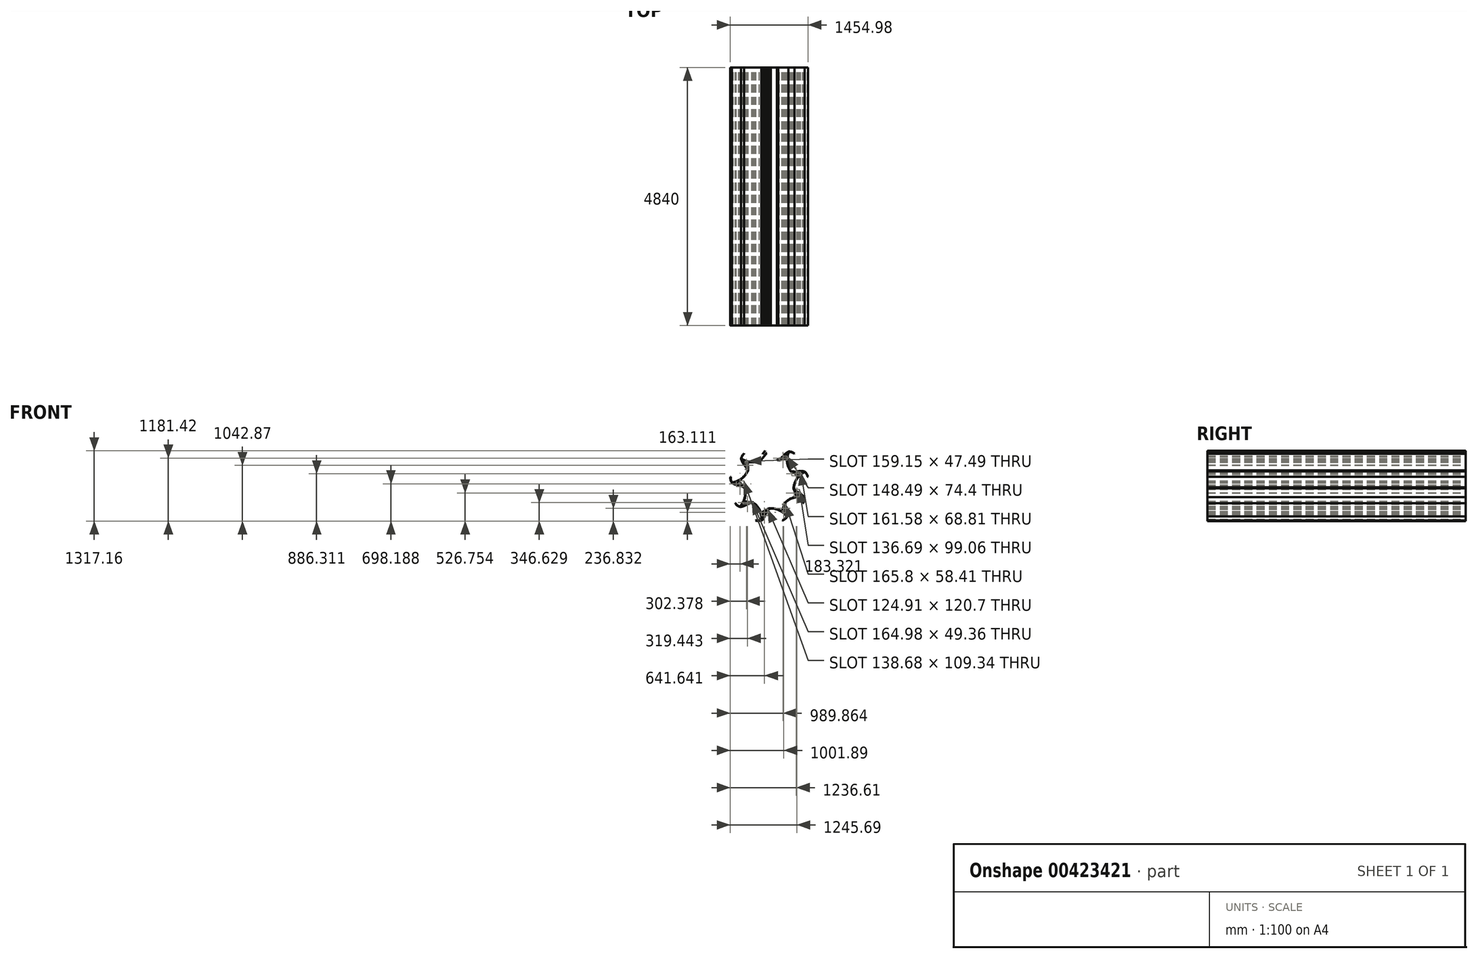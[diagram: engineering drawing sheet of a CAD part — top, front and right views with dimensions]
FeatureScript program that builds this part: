
annotation { "Feature Type Name" : "Feature", "Feature Type Description" : "" }
export const myFeature = defineFeature(function(context is Context, id is Id, definition is map)
    precondition{}
    {
        {
            var Q0;
            Q0=qCreatedBy(makeId("Front.planeOp"),FACE);
            var sketch = newSketch(context, id + "F0", { "sketchPlane" : qUnion([Q0])});
            skCircle(sketch, "E0", {"center": v(0, 0) * mm, "radius": 462.5 * mm, "construction": true});
            skLineSegment(sketch, "E1", {"start": v(0, 0) * mm, "end": v(0, 462.5) * mm, "construction": true});
            skPoint(sketch, "E2", {"position": v(0, 737.5) * mm});
            skPoint(sketch, "E3", {"position": v(-110, 692.5) * mm});
            skPoint(sketch, "E4", {"position": v(0, 729.5) * mm});
            skPoint(sketch, "E5", {"position": v(-97, 692.5) * mm});
            skPoint(sketch, "E6", {"position": v(-172.02, 429.32) * mm});
            skLineSegment(sketch, "E7", {"start": v(0, 0) * mm, "end": v(-172.02, 429.32) * mm, "construction": true});
            skLineSegment(sketch, "E8", {"start": v(-172.02, 429.32) * mm, "end": v(-176.48, 440.46) * mm, "construction": true});
            skPoint(sketch, "E9", {"position": v(-174.25, 434.9) * mm});
            skArc(sketch, "E10", {"start": v(-174.25, 434.9) * mm, "mid": v(-160.23, 440.25) * mm, "end": v(-146.06, 445.15) * mm});
            skArc(sketch, "E11", {"start": v(-176.48, 440.46) * mm, "mid": v(-166.98, 444.15) * mm, "end": v(-157.4, 447.63) * mm});
            skLineSegment(sketch, "E12", {"start": v(-176.48, 440.46) * mm, "end": v(-174.25, 434.9) * mm});
            skLineSegment(sketch, "E13", {"start": v(0, 0) * mm, "end": v(-146.06, 445.15) * mm, "construction": true});
            skLineSegment(sketch, "E14", {"start": v(-146.06, 445.15) * mm, "end": v(-148.66, 453.08) * mm, "construction": true});
            skPoint(sketch, "E15.MirrorP", {"position": v(172.02, 429.32) * mm});
            skPoint(sketch, "E16.MirrorP", {"position": v(174.25, 434.9) * mm});
            skLineSegment(sketch, "E17.MirrorCS", {"start": v(146.06, 445.15) * mm, "end": v(148.66, 453.08) * mm, "construction": true});
            skLineSegment(sketch, "E18.MirrorCS", {"start": v(172.02, 429.32) * mm, "end": v(176.48, 440.46) * mm, "construction": true});
            skLineSegment(sketch, "E19.MirrorCS", {"start": v(0, 0) * mm, "end": v(172.02, 429.32) * mm, "construction": true});
            skLineSegment(sketch, "E20.MirrorCS", {"start": v(0, 0) * mm, "end": v(146.06, 445.15) * mm, "construction": true});
            skArc(sketch, "E21", {"start": v(146.06, 445.15) * mm, "mid": v(160.23, 440.25) * mm, "end": v(174.25, 434.9) * mm});
            skLineSegment(sketch, "E22", {"start": v(174.25, 434.9) * mm, "end": v(172.02, 429.32) * mm});
            skPoint(sketch, "E23", {"position": v(131.78, 443.33) * mm});
            skPoint(sketch, "E24", {"position": v(144.19, 439.45) * mm});
            skArc(sketch, "E25", {"start": v(131.78, 443.33) * mm, "mid": v(152.06, 436.79) * mm, "end": v(172.02, 429.32) * mm});
            skLineSegment(sketch, "E26", {"start": v(-157.4, 692.5) * mm, "end": v(-110, 692.5) * mm, "construction": true});
            skPoint(sketch, "E27", {"position": v(-133.7, 692.5) * mm});
            skLineSegment(sketch, "E28", {"start": v(-157.4, 692.5) * mm, "end": v(-157.4, 447.63) * mm, "construction": true});
            skPoint(sketch, "E29", {"position": v(-157.4, 570.07) * mm});
            skPoint(sketch, "E30", {"position": v(-133.7, 570.07) * mm});
            skArc(sketch, "E31", {"start": v(-157.4, 447.63) * mm, "mid": v(-139.68, 507.71) * mm, "end": v(-133.7, 570.07) * mm});
            skArc(sketch, "E32", {"start": v(-110, 692.5) * mm, "mid": v(-127.72, 632.42) * mm, "end": v(-133.7, 570.07) * mm});
            skArc(sketch, "E33", {"start": v(0, 737.5) * mm, "mid": v(-59.42, 725.82) * mm, "end": v(-110, 692.5) * mm});
            skLineSegment(sketch, "E34", {"start": v(0, 737.5) * mm, "end": v(0, 729.5) * mm});
            skArc(sketch, "E35", {"start": v(0, 729.5) * mm, "mid": v(-51.9, 719.94) * mm, "end": v(-97, 692.5) * mm});
            skArc(sketch, "E36", {"start": v(-97, 692.5) * mm, "mid": v(-5.55, 539.27) * mm, "end": v(146.06, 445.15) * mm});
            skArc(sketch, "E37", {"start": v(-146.06, 445.15) * mm, "mid": v(-127.1, 506.34) * mm, "end": v(-120.7, 570.07) * mm});
            skArc(sketch, "E38", {"start": v(-103.63, 668.34) * mm, "mid": v(-116.4, 619.94) * mm, "end": v(-120.7, 570.07) * mm});
            skPoint(sketch, "E39", {"position": v(-118.63, 668.34) * mm});
            skPoint(sketch, "E40", {"position": v(-88.63, 668.34) * mm});
            skLineSegment(sketch, "E41", {"start": v(-118.63, 668.34) * mm, "end": v(-88.63, 668.34) * mm, "construction": true});
            skArc(sketch, "E42", {"start": v(-103.63, 668.34) * mm, "mid": v(-10.1, 530.54) * mm, "end": v(131.78, 443.33) * mm});
            skLineSegment(sketch, "E43", {"start": v(-146.06, 445.15) * mm, "end": v(-47.75, 572) * mm});
            skLineSegment(sketch, "E44", {"start": v(-50.29, 575.26) * mm, "end": v(-140.74, 458.55) * mm});
            skLineSegment(sketch, "E45", {"start": v(-121.26, 551.05) * mm, "end": v(-74.81, 611) * mm});
            skLineSegment(sketch, "E46", {"start": v(-120.92, 558.02) * mm, "end": v(-77.02, 614.67) * mm});
            skPoint(sketch, "E47.1.0", {"position": v(-520.48, 435.72) * mm});
            skPoint(sketch, "E47.1.1", {"position": v(-547.55, 444.55) * mm});
            skArc(sketch, "E47.1.2", {"start": v(-474.06, 564.96) * mm, "mid": v(-512.07, 517.8) * mm, "end": v(-529.4, 459.78) * mm});
            skPoint(sketch, "E47.1.3", {"position": v(-468.91, 558.83) * mm});
            skLineSegment(sketch, "E47.1.5", {"start": v(-398.02, 247.12) * mm, "end": v(-404.26, 407.48) * mm});
            skArc(sketch, "E47.1.6", {"start": v(-398.02, 247.12) * mm, "mid": v(-422.83, 306.18) * mm, "end": v(-458.9, 359.11) * mm});
            skPoint(sketch, "E47.1.7", {"position": v(-497.5, 455) * mm});
            skPoint(sketch, "E47.1.8", {"position": v(-413.02, 221.14) * mm});
            skLineSegment(sketch, "E47.1.9", {"start": v(-447.1, 344.18) * mm, "end": v(-450.05, 419.96) * mm});
            skPoint(sketch, "E47.1.10", {"position": v(-474.06, 564.96) * mm});
            skArc(sketch, "E47.1.11", {"start": v(-519.44, 468.14) * mm, "mid": v(-350.89, 409.54) * mm, "end": v(-174.25, 434.89) * mm});
            skPoint(sketch, "E47.1.12", {"position": v(-487, 335.53) * mm});
            skLineSegment(sketch, "E47.1.13", {"start": v(-565.7, 429.31) * mm, "end": v(-408.3, 241.74) * mm, "construction": true});
            skPoint(sketch, "E47.1.14", {"position": v(-146.06, 445.15) * mm});
            skLineSegment(sketch, "E47.1.15", {"start": v(-408.3, 408.35) * mm, "end": v(-402.56, 260.8) * mm});
            skArc(sketch, "E47.1.16", {"start": v(-509, 445.37) * mm, "mid": v(-348.77, 399.92) * mm, "end": v(-184.02, 424.31) * mm});
            skArc(sketch, "E47.1.17", {"start": v(-529.4, 459.78) * mm, "mid": v(-504.35, 402.37) * mm, "end": v(-468.85, 350.76) * mm});
            skPoint(sketch, "E47.1.18", {"position": v(-529.4, 459.78) * mm});
            skPoint(sketch, "E47.1.19", {"position": v(-184.02, 424.31) * mm});
            skPoint(sketch, "E47.1.20", {"position": v(-468.85, 350.76) * mm});
            skPoint(sketch, "E47.1.21", {"position": v(-519.44, 468.14) * mm});
            skArc(sketch, "E47.1.22", {"start": v(-509, 445.37) * mm, "mid": v(-487.66, 400.08) * mm, "end": v(-458.9, 359.11) * mm});
            skLineSegment(sketch, "E47.1.23", {"start": v(-451.32, 349.74) * mm, "end": v(-454.1, 421.35) * mm});
            skArc(sketch, "E47.1.24", {"start": v(-408.3, 241.74) * mm, "mid": v(-433.35, 299.15) * mm, "end": v(-468.85, 350.76) * mm});
            skArc(sketch, "E47.1.25", {"start": v(-468.91, 558.83) * mm, "mid": v(-502.53, 518.14) * mm, "end": v(-519.44, 468.14) * mm});
            skPoint(sketch, "E47.1.26", {"position": v(-407.73, 218.31) * mm});
            skLineSegment(sketch, "E47.1.27", {"start": v(-565.7, 429.31) * mm, "end": v(-529.4, 459.78) * mm, "construction": true});
            skPoint(sketch, "E47.1.28", {"position": v(-144.2, 439.45) * mm});
            skLineSegment(sketch, "E47.1.29", {"start": v(-520.48, 435.72) * mm, "end": v(-497.5, 455) * mm, "construction": true});
            skArc(sketch, "E47.1.30", {"start": v(-184.02, 424.31) * mm, "mid": v(-164.28, 432.34) * mm, "end": v(-144.2, 439.45) * mm});
            skLineSegment(sketch, "E47.1.31", {"start": v(-474.06, 564.96) * mm, "end": v(-468.91, 558.83) * mm});
            skArc(sketch, "E47.1.32", {"start": v(-174.25, 434.89) * mm, "mid": v(-160.24, 440.24) * mm, "end": v(-146.06, 445.15) * mm});
            skLineSegment(sketch, "E47.1.33", {"start": v(-407.73, 218.31) * mm, "end": v(-418.31, 223.97) * mm, "construction": true});
            skArc(sketch, "E47.1.34", {"start": v(-418.31, 223.97) * mm, "mid": v(-413.4, 232.9) * mm, "end": v(-408.3, 241.74) * mm});
            skArc(sketch, "E47.1.35", {"start": v(-413.02, 221.14) * mm, "mid": v(-405.73, 234.25) * mm, "end": v(-398.02, 247.12) * mm});
            skLineSegment(sketch, "E47.1.36", {"start": v(-418.31, 223.97) * mm, "end": v(-413.02, 221.14) * mm});
            skLineSegment(sketch, "E47.1.37", {"start": v(-174.25, 434.89) * mm, "end": v(-177.36, 442.64) * mm, "construction": true});
            skLineSegment(sketch, "E47.1.38", {"start": v(-398.02, 247.12) * mm, "end": v(-405.12, 251.53) * mm, "construction": true});
            skLineSegment(sketch, "E47.1.39", {"start": v(-146.06, 445.15) * mm, "end": v(-144.2, 439.45) * mm});
            skLineSegment(sketch, "E47.1.40", {"start": v(-144.2, 439.45) * mm, "end": v(-147.93, 450.85) * mm, "construction": true});
            skPoint(sketch, "E47.2.0", {"position": v(-678.8, -0.78) * mm});
            skPoint(sketch, "E47.2.1", {"position": v(-705.2, -11.42) * mm});
            skArc(sketch, "E47.2.2", {"start": v(-726.3, 128.07) * mm, "mid": v(-725.1, 67.51) * mm, "end": v(-701.08, 11.92) * mm});
            skPoint(sketch, "E47.2.3", {"position": v(-718.42, 126.68) * mm});
            skPoint(sketch, "E47.2.4", {"position": v(-407.74, 218.3) * mm});
            skLineSegment(sketch, "E47.2.5", {"start": v(-463.75, -66.54) * mm, "end": v(-571.6, 52.3) * mm});
            skArc(sketch, "E47.2.6", {"start": v(-463.75, -66.54) * mm, "mid": v(-520.71, -37.25) * mm, "end": v(-582.37, -19.87) * mm});
            skPoint(sketch, "E47.2.7", {"position": v(-673.58, 28.77) * mm});
            skPoint(sketch, "E47.2.8", {"position": v(-458.54, -96.08) * mm});
            skLineSegment(sketch, "E47.2.9", {"start": v(-563.73, -23.73) * mm, "end": v(-614.7, 32.42) * mm});
            skPoint(sketch, "E47.2.10", {"position": v(-726.3, 128.07) * mm});
            skArc(sketch, "E47.2.11", {"start": v(-698.82, 24.73) * mm, "mid": v(-532.04, 88.18) * mm, "end": v(-413.03, 221.14) * mm});
            skPoint(sketch, "E47.2.12", {"position": v(-588.74, -56.01) * mm});
            skLineSegment(sketch, "E47.2.13", {"start": v(-709.31, -34.75) * mm, "end": v(-468.17, -77.27) * mm, "construction": true});
            skPoint(sketch, "E47.2.14", {"position": v(-398.03, 247.12) * mm});
            skLineSegment(sketch, "E47.2.15", {"start": v(-575.25, 50.37) * mm, "end": v(-476.02, -58.97) * mm});
            skArc(sketch, "E47.2.16", {"start": v(-676.19, 14) * mm, "mid": v(-524.24, 82.18) * mm, "end": v(-413.71, 206.76) * mm});
            skArc(sketch, "E47.2.17", {"start": v(-701.08, 11.92) * mm, "mid": v(-645, -15.96) * mm, "end": v(-584.62, -32.68) * mm});
            skPoint(sketch, "E47.2.18", {"position": v(-701.08, 11.92) * mm});
            skPoint(sketch, "E47.2.19", {"position": v(-413.71, 206.76) * mm});
            skPoint(sketch, "E47.2.20", {"position": v(-584.62, -32.68) * mm});
            skPoint(sketch, "E47.2.21", {"position": v(-698.82, 24.73) * mm});
            skArc(sketch, "E47.2.22", {"start": v(-676.19, 14) * mm, "mid": v(-630.74, -6.98) * mm, "end": v(-582.37, -19.87) * mm});
            skLineSegment(sketch, "E47.2.23", {"start": v(-570.54, -22.19) * mm, "end": v(-618.7, 30.88) * mm});
            skArc(sketch, "E47.2.24", {"start": v(-468.17, -77.27) * mm, "mid": v(-524.26, -49.4) * mm, "end": v(-584.62, -32.68) * mm});
            skArc(sketch, "E47.2.25", {"start": v(-718.42, 126.68) * mm, "mid": v(-718.01, 73.9) * mm, "end": v(-698.82, 24.73) * mm});
            skPoint(sketch, "E47.2.26", {"position": v(-452.67, -94.85) * mm});
            skLineSegment(sketch, "E47.2.27", {"start": v(-709.31, -34.75) * mm, "end": v(-701.08, 11.92) * mm, "construction": true});
            skPoint(sketch, "E47.2.28", {"position": v(-392.93, 243.95) * mm});
            skLineSegment(sketch, "E47.2.29", {"start": v(-678.8, -0.78) * mm, "end": v(-673.58, 28.77) * mm, "construction": true});
            skArc(sketch, "E47.2.30", {"start": v(-413.71, 206.76) * mm, "mid": v(-403.75, 225.6) * mm, "end": v(-392.93, 243.95) * mm});
            skLineSegment(sketch, "E47.2.31", {"start": v(-726.3, 128.07) * mm, "end": v(-718.42, 126.68) * mm});
            skArc(sketch, "E47.2.32", {"start": v(-413.03, 221.14) * mm, "mid": v(-405.73, 234.25) * mm, "end": v(-398.03, 247.12) * mm});
            skLineSegment(sketch, "E47.2.33", {"start": v(-452.67, -94.85) * mm, "end": v(-464.41, -97.31) * mm, "construction": true});
            skArc(sketch, "E47.2.34", {"start": v(-464.41, -97.31) * mm, "mid": v(-466.4, -87.31) * mm, "end": v(-468.17, -77.27) * mm});
            skArc(sketch, "E47.2.35", {"start": v(-458.54, -96.08) * mm, "mid": v(-461.38, -81.35) * mm, "end": v(-463.75, -66.54) * mm});
            skLineSegment(sketch, "E47.2.36", {"start": v(-464.41, -97.31) * mm, "end": v(-458.54, -96.08) * mm});
            skLineSegment(sketch, "E47.2.37", {"start": v(-413.03, 221.14) * mm, "end": v(-420.39, 225.08) * mm, "construction": true});
            skLineSegment(sketch, "E47.2.38", {"start": v(-463.75, -66.54) * mm, "end": v(-472.02, -67.72) * mm, "construction": true});
            skLineSegment(sketch, "E47.2.39", {"start": v(-398.03, 247.12) * mm, "end": v(-392.93, 243.95) * mm});
            skLineSegment(sketch, "E47.2.40", {"start": v(-392.93, 243.95) * mm, "end": v(-403.12, 250.28) * mm, "construction": true});
            skPoint(sketch, "E47.3.0", {"position": v(-519.49, -436.91) * mm});
            skPoint(sketch, "E47.3.1", {"position": v(-532.87, -462.04) * mm});
            skArc(sketch, "E47.3.2", {"start": v(-638.7, -368.75) * mm, "mid": v(-598.86, -414.37) * mm, "end": v(-544.72, -441.51) * mm});
            skPoint(sketch, "E47.3.3", {"position": v(-631.77, -364.75) * mm});
            skPoint(sketch, "E47.3.4", {"position": v(-452.67, -94.86) * mm});
            skLineSegment(sketch, "E47.3.5", {"start": v(-312.48, -349.06) * mm, "end": v(-471.5, -327.36) * mm});
            skArc(sketch, "E47.3.6", {"start": v(-312.48, -349.06) * mm, "mid": v(-374.95, -363.24) * mm, "end": v(-433.34, -389.56) * mm});
            skPoint(sketch, "E47.3.7", {"position": v(-534.49, -410.93) * mm});
            skPoint(sketch, "E47.3.8", {"position": v(-289.5, -368.35) * mm});
            skLineSegment(sketch, "E47.3.9", {"start": v(-416.6, -380.54) * mm, "end": v(-491.73, -370.28) * mm});
            skPoint(sketch, "E47.3.10", {"position": v(-638.7, -368.75) * mm});
            skArc(sketch, "E47.3.11", {"start": v(-551.22, -430.25) * mm, "mid": v(-464.25, -274.44) * mm, "end": v(-458.54, -96.09) * mm});
            skPoint(sketch, "E47.3.12", {"position": v(-415, -421.34) * mm});
            skLineSegment(sketch, "E47.3.13", {"start": v(-521.02, -482.56) * mm, "end": v(-308.97, -360.13) * mm, "construction": true});
            skPoint(sketch, "E47.3.14", {"position": v(-463.75, -66.54) * mm});
            skLineSegment(sketch, "E47.3.15", {"start": v(-473.05, -331.18) * mm, "end": v(-326.75, -351.15) * mm});
            skArc(sketch, "E47.3.16", {"start": v(-526.99, -423.92) * mm, "mid": v(-454.41, -274.02) * mm, "end": v(-449.82, -107.54) * mm});
            skArc(sketch, "E47.3.17", {"start": v(-544.72, -441.51) * mm, "mid": v(-483.83, -426.82) * mm, "end": v(-426.84, -400.82) * mm});
            skPoint(sketch, "E47.3.18", {"position": v(-544.72, -441.51) * mm});
            skPoint(sketch, "E47.3.19", {"position": v(-449.82, -107.54) * mm});
            skPoint(sketch, "E47.3.20", {"position": v(-426.84, -400.82) * mm});
            skPoint(sketch, "E47.3.21", {"position": v(-551.22, -430.25) * mm});
            skArc(sketch, "E47.3.22", {"start": v(-526.99, -423.92) * mm, "mid": v(-478.68, -410.78) * mm, "end": v(-433.34, -389.56) * mm});
            skLineSegment(sketch, "E47.3.23", {"start": v(-422.8, -383.73) * mm, "end": v(-493.8, -374.04) * mm});
            skArc(sketch, "E47.3.24", {"start": v(-308.97, -360.13) * mm, "mid": v(-369.86, -374.82) * mm, "end": v(-426.84, -400.82) * mm});
            skArc(sketch, "E47.3.25", {"start": v(-631.77, -364.75) * mm, "mid": v(-597.53, -404.92) * mm, "end": v(-551.22, -430.25) * mm});
            skPoint(sketch, "E47.3.26", {"position": v(-285.8, -363.63) * mm});
            skLineSegment(sketch, "E47.3.27", {"start": v(-521.02, -482.56) * mm, "end": v(-544.72, -441.51) * mm, "construction": true});
            skPoint(sketch, "E47.3.28", {"position": v(-457.81, -65.7) * mm});
            skLineSegment(sketch, "E47.3.29", {"start": v(-519.49, -436.91) * mm, "end": v(-534.49, -410.93) * mm, "construction": true});
            skArc(sketch, "E47.3.30", {"start": v(-449.82, -107.54) * mm, "mid": v(-454.3, -86.7) * mm, "end": v(-457.81, -65.7) * mm});
            skLineSegment(sketch, "E47.3.31", {"start": v(-638.7, -368.75) * mm, "end": v(-631.77, -364.75) * mm});
            skArc(sketch, "E47.3.32", {"start": v(-458.54, -96.09) * mm, "mid": v(-461.38, -81.36) * mm, "end": v(-463.75, -66.54) * mm});
            skLineSegment(sketch, "E47.3.33", {"start": v(-285.8, -363.63) * mm, "end": v(-293.21, -373.07) * mm, "construction": true});
            skArc(sketch, "E47.3.34", {"start": v(-293.21, -373.07) * mm, "mid": v(-301.16, -366.68) * mm, "end": v(-308.97, -360.13) * mm});
            skArc(sketch, "E47.3.35", {"start": v(-289.5, -368.35) * mm, "mid": v(-301.15, -358.89) * mm, "end": v(-312.48, -349.06) * mm});
            skLineSegment(sketch, "E47.3.36", {"start": v(-293.21, -373.07) * mm, "end": v(-289.5, -368.35) * mm});
            skLineSegment(sketch, "E47.3.37", {"start": v(-458.54, -96.09) * mm, "end": v(-466.71, -97.8) * mm, "construction": true});
            skLineSegment(sketch, "E47.3.38", {"start": v(-312.48, -349.06) * mm, "end": v(-318.05, -355.28) * mm, "construction": true});
            skLineSegment(sketch, "E47.3.39", {"start": v(-463.75, -66.54) * mm, "end": v(-457.81, -65.7) * mm});
            skLineSegment(sketch, "E47.3.40", {"start": v(-457.81, -65.7) * mm, "end": v(-469.69, -67.4) * mm, "construction": true});
            skPoint(sketch, "E47.4.0", {"position": v(-117.1, -668.61) * mm});
            skPoint(sketch, "E47.4.1", {"position": v(-111.21, -696.46) * mm});
            skArc(sketch, "E47.4.2", {"start": v(-252.24, -693.02) * mm, "mid": v(-192.4, -702.37) * mm, "end": v(-133.48, -688.36) * mm});
            skPoint(sketch, "E47.4.3", {"position": v(-249.5, -685.5) * mm});
            skPoint(sketch, "E47.4.4", {"position": v(-285.8, -363.63) * mm});
            skLineSegment(sketch, "E47.4.5", {"start": v(-15, -468.26) * mm, "end": v(-150.76, -553.84) * mm});
            skArc(sketch, "E47.4.6", {"start": v(-15, -468.26) * mm, "mid": v(-53.74, -519.27) * mm, "end": v(-81.56, -576.97) * mm});
            skPoint(sketch, "E47.4.7", {"position": v(-145.3, -658.35) * mm});
            skPoint(sketch, "E47.4.8", {"position": v(15, -468.26) * mm});
            skLineSegment(sketch, "E47.4.9", {"start": v(-74.52, -559.3) * mm, "end": v(-138.67, -599.73) * mm});
            skPoint(sketch, "E47.4.10", {"position": v(-252.24, -693.02) * mm});
            skArc(sketch, "E47.4.11", {"start": v(-145.7, -683.91) * mm, "mid": v(-179.23, -508.65) * mm, "end": v(-289.5, -368.35) * mm});
            skPoint(sketch, "E47.4.12", {"position": v(-47.07, -589.52) * mm});
            skLineSegment(sketch, "E47.4.13", {"start": v(-88.95, -704.57) * mm, "end": v(-5.2, -474.47) * mm, "construction": true});
            skPoint(sketch, "E47.4.14", {"position": v(-312.48, -349.07) * mm});
            skLineSegment(sketch, "E47.4.15", {"start": v(-149.5, -557.77) * mm, "end": v(-24.58, -479.03) * mm});
            skArc(sketch, "E47.4.16", {"start": v(-131.2, -663.48) * mm, "mid": v(-171.96, -502) * mm, "end": v(-275.46, -371.52) * mm});
            skArc(sketch, "E47.4.17", {"start": v(-133.48, -688.36) * mm, "mid": v(-96.28, -637.96) * mm, "end": v(-69.34, -581.42) * mm});
            skPoint(sketch, "E47.4.18", {"position": v(-133.48, -688.36) * mm});
            skPoint(sketch, "E47.4.19", {"position": v(-275.46, -371.52) * mm});
            skPoint(sketch, "E47.4.20", {"position": v(-69.34, -581.42) * mm});
            skPoint(sketch, "E47.4.21", {"position": v(-145.7, -683.91) * mm});
            skArc(sketch, "E47.4.22", {"start": v(-131.2, -663.48) * mm, "mid": v(-102.65, -622.36) * mm, "end": v(-81.56, -576.97) * mm});
            skLineSegment(sketch, "E47.4.23", {"start": v(-77.22, -565.72) * mm, "end": v(-137.85, -603.94) * mm});
            skArc(sketch, "E47.4.24", {"start": v(-5.2, -474.47) * mm, "mid": v(-42.4, -524.87) * mm, "end": v(-69.34, -581.42) * mm});
            skArc(sketch, "E47.4.25", {"start": v(-249.5, -685.5) * mm, "mid": v(-197.45, -694.27) * mm, "end": v(-145.7, -683.91) * mm});
            skPoint(sketch, "E47.4.26", {"position": v(14.8, -462.26) * mm});
            skLineSegment(sketch, "E47.4.27", {"start": v(-88.95, -704.57) * mm, "end": v(-133.48, -688.36) * mm, "construction": true});
            skPoint(sketch, "E47.4.28", {"position": v(-308.48, -344.6) * mm});
            skLineSegment(sketch, "E47.4.29", {"start": v(-117.1, -668.61) * mm, "end": v(-145.3, -658.35) * mm, "construction": true});
            skArc(sketch, "E47.4.30", {"start": v(-275.46, -371.52) * mm, "mid": v(-292.28, -358.44) * mm, "end": v(-308.48, -344.6) * mm});
            skLineSegment(sketch, "E47.4.31", {"start": v(-252.24, -693.02) * mm, "end": v(-249.5, -685.5) * mm});
            skArc(sketch, "E47.4.32", {"start": v(-289.5, -368.35) * mm, "mid": v(-301.14, -358.9) * mm, "end": v(-312.48, -349.07) * mm});
            skLineSegment(sketch, "E47.4.33", {"start": v(14.8, -462.26) * mm, "end": v(15.19, -474.26) * mm, "construction": true});
            skArc(sketch, "E47.4.34", {"start": v(15.19, -474.26) * mm, "mid": v(5, -474.47) * mm, "end": v(-5.2, -474.47) * mm});
            skArc(sketch, "E47.4.35", {"start": v(15, -468.26) * mm, "mid": v(0, -468.5) * mm, "end": v(-15, -468.26) * mm});
            skLineSegment(sketch, "E47.4.36", {"start": v(15.19, -474.26) * mm, "end": v(15, -468.26) * mm});
            skLineSegment(sketch, "E47.4.37", {"start": v(-289.5, -368.35) * mm, "end": v(-294.66, -374.92) * mm, "construction": true});
            skLineSegment(sketch, "E47.4.38", {"start": v(-15, -468.26) * mm, "end": v(-15.27, -476.6) * mm, "construction": true});
            skLineSegment(sketch, "E47.4.39", {"start": v(-312.48, -349.07) * mm, "end": v(-308.48, -344.6) * mm});
            skLineSegment(sketch, "E47.4.40", {"start": v(-308.48, -344.6) * mm, "end": v(-316.48, -353.54) * mm, "construction": true});
            skPoint(sketch, "E47.5.0", {"position": v(340.07, -587.46) * mm});
            skPoint(sketch, "E47.5.1", {"position": v(362.48, -605) * mm});
            skArc(sketch, "E47.5.2", {"start": v(252.24, -693.02) * mm, "mid": v(304.08, -661.72) * mm, "end": v(340.22, -613.11) * mm});
            skPoint(sketch, "E47.5.3", {"position": v(249.5, -685.5) * mm});
            skPoint(sketch, "E47.5.4", {"position": v(14.81, -462.26) * mm});
            skLineSegment(sketch, "E47.5.5", {"start": v(289.5, -368.35) * mm, "end": v(240.5, -521.17) * mm});
            skArc(sketch, "E47.5.6", {"start": v(289.5, -368.35) * mm, "mid": v(292.61, -432.33) * mm, "end": v(308.4, -494.4) * mm});
            skPoint(sketch, "E47.5.7", {"position": v(311.88, -597.72) * mm});
            skPoint(sketch, "E47.5.8", {"position": v(312.48, -349.07) * mm});
            skLineSegment(sketch, "E47.5.9", {"start": v(302.42, -476.34) * mm, "end": v(279.27, -548.56) * mm});
            skPoint(sketch, "E47.5.10", {"position": v(252.24, -693.02) * mm});
            skArc(sketch, "E47.5.11", {"start": v(328, -617.56) * mm, "mid": v(189.66, -504.85) * mm, "end": v(15, -468.26) * mm});
            skPoint(sketch, "E47.5.12", {"position": v(342.88, -481.86) * mm});
            skLineSegment(sketch, "E47.5.13", {"start": v(384.75, -596.9) * mm, "end": v(301, -366.8) * mm, "construction": true});
            skPoint(sketch, "E47.5.14", {"position": v(-15, -468.26) * mm});
            skLineSegment(sketch, "E47.5.15", {"start": v(244, -523.37) * mm, "end": v(289.08, -382.76) * mm});
            skArc(sketch, "E47.5.16", {"start": v(325.97, -592.6) * mm, "mid": v(190.95, -495.1) * mm, "end": v(27.8, -461.66) * mm});
            skArc(sketch, "E47.5.17", {"start": v(340.22, -613.11) * mm, "mid": v(336.32, -550.6) * mm, "end": v(320.6, -489.96) * mm});
            skPoint(sketch, "E47.5.18", {"position": v(340.22, -613.11) * mm});
            skPoint(sketch, "E47.5.19", {"position": v(27.8, -461.66) * mm});
            skPoint(sketch, "E47.5.20", {"position": v(320.6, -489.96) * mm});
            skPoint(sketch, "E47.5.21", {"position": v(328, -617.56) * mm});
            skArc(sketch, "E47.5.22", {"start": v(325.97, -592.6) * mm, "mid": v(321.41, -542.74) * mm, "end": v(308.4, -494.4) * mm});
            skLineSegment(sketch, "E47.5.23", {"start": v(304.48, -483) * mm, "end": v(282.6, -551.26) * mm});
            skArc(sketch, "E47.5.24", {"start": v(301, -366.8) * mm, "mid": v(304.9, -429.32) * mm, "end": v(320.6, -489.96) * mm});
            skArc(sketch, "E47.5.25", {"start": v(249.5, -685.5) * mm, "mid": v(295.01, -658.76) * mm, "end": v(328, -617.56) * mm});
            skPoint(sketch, "E47.5.26", {"position": v(308.48, -344.6) * mm});
            skLineSegment(sketch, "E47.5.27", {"start": v(384.75, -596.9) * mm, "end": v(340.22, -613.11) * mm, "construction": true});
            skPoint(sketch, "E47.5.28", {"position": v(-14.8, -462.26) * mm});
            skLineSegment(sketch, "E47.5.29", {"start": v(340.07, -587.46) * mm, "end": v(311.88, -597.72) * mm, "construction": true});
            skArc(sketch, "E47.5.30", {"start": v(27.8, -461.66) * mm, "mid": v(6.5, -462.45) * mm, "end": v(-14.8, -462.26) * mm});
            skLineSegment(sketch, "E47.5.31", {"start": v(252.24, -693.02) * mm, "end": v(249.5, -685.5) * mm});
            skArc(sketch, "E47.5.32", {"start": v(15, -468.26) * mm, "mid": v(0, -468.5) * mm, "end": v(-15, -468.26) * mm});
            skLineSegment(sketch, "E47.5.33", {"start": v(308.48, -344.6) * mm, "end": v(316.48, -353.54) * mm, "construction": true});
            skArc(sketch, "E47.5.34", {"start": v(316.48, -353.54) * mm, "mid": v(308.81, -360.26) * mm, "end": v(301, -366.8) * mm});
            skArc(sketch, "E47.5.35", {"start": v(312.48, -349.07) * mm, "mid": v(301.14, -358.9) * mm, "end": v(289.5, -368.35) * mm});
            skLineSegment(sketch, "E47.5.36", {"start": v(316.48, -353.54) * mm, "end": v(312.48, -349.07) * mm});
            skLineSegment(sketch, "E47.5.37", {"start": v(15, -468.26) * mm, "end": v(15.27, -476.6) * mm, "construction": true});
            skLineSegment(sketch, "E47.5.38", {"start": v(289.5, -368.35) * mm, "end": v(294.66, -374.92) * mm, "construction": true});
            skLineSegment(sketch, "E47.5.39", {"start": v(-15, -468.26) * mm, "end": v(-14.8, -462.26) * mm});
            skLineSegment(sketch, "E47.5.40", {"start": v(-14.8, -462.26) * mm, "end": v(-15.19, -474.26) * mm, "construction": true});
            skPoint(sketch, "E47.6.0", {"position": v(638.12, -231.43) * mm});
            skPoint(sketch, "E47.6.1", {"position": v(666.57, -230.46) * mm});
            skArc(sketch, "E47.6.2", {"start": v(638.7, -368.75) * mm, "mid": v(658.29, -311.44) * mm, "end": v(654.72, -250.99) * mm});
            skPoint(sketch, "E47.6.3", {"position": v(631.77, -364.75) * mm});
            skPoint(sketch, "E47.6.4", {"position": v(308.48, -344.6) * mm});
            skLineSegment(sketch, "E47.6.5", {"start": v(458.54, -96.09) * mm, "end": v(519.24, -244.65) * mm});
            skArc(sketch, "E47.6.6", {"start": v(458.54, -96.09) * mm, "mid": v(502.05, -143.1) * mm, "end": v(554.04, -180.5) * mm});
            skPoint(sketch, "E47.6.7", {"position": v(623.12, -257.41) * mm});
            skPoint(sketch, "E47.6.8", {"position": v(463.75, -66.54) * mm});
            skLineSegment(sketch, "E47.6.9", {"start": v(537.85, -170.5) * mm, "end": v(566.54, -240.7) * mm});
            skPoint(sketch, "E47.6.10", {"position": v(638.7, -368.75) * mm});
            skArc(sketch, "E47.6.11", {"start": v(648.22, -262.25) * mm, "mid": v(469.8, -264.83) * mm, "end": v(312.48, -349.06) * mm});
            skPoint(sketch, "E47.6.12", {"position": v(572.4, -148.73) * mm});
            skLineSegment(sketch, "E47.6.13", {"start": v(678.42, -209.94) * mm, "end": v(466.36, -87.5) * mm, "construction": true});
            skPoint(sketch, "E47.6.14", {"position": v(289.5, -368.35) * mm});
            skLineSegment(sketch, "E47.6.15", {"start": v(523.33, -244.08) * mm, "end": v(467.48, -107.4) * mm});
            skArc(sketch, "E47.6.16", {"start": v(630.62, -244.42) * mm, "mid": v(464.52, -256.52) * mm, "end": v(318.05, -335.79) * mm});
            skArc(sketch, "E47.6.17", {"start": v(654.72, -250.99) * mm, "mid": v(611.55, -205.6) * mm, "end": v(560.54, -169.25) * mm});
            skPoint(sketch, "E47.6.18", {"position": v(654.72, -250.99) * mm});
            skPoint(sketch, "E47.6.19", {"position": v(318.05, -335.79) * mm});
            skPoint(sketch, "E47.6.20", {"position": v(560.54, -169.25) * mm});
            skPoint(sketch, "E47.6.21", {"position": v(648.22, -262.25) * mm});
            skArc(sketch, "E47.6.22", {"start": v(630.62, -244.42) * mm, "mid": v(595.08, -209.16) * mm, "end": v(554.04, -180.5) * mm});
            skLineSegment(sketch, "E47.6.23", {"start": v(543.72, -174.28) * mm, "end": v(570.83, -240.63) * mm});
            skArc(sketch, "E47.6.24", {"start": v(466.36, -87.5) * mm, "mid": v(509.53, -132.9) * mm, "end": v(560.54, -169.25) * mm});
            skArc(sketch, "E47.6.25", {"start": v(631.77, -364.75) * mm, "mid": v(649.44, -315.01) * mm, "end": v(648.22, -262.25) * mm});
            skPoint(sketch, "E47.6.26", {"position": v(457.81, -65.7) * mm});
            skLineSegment(sketch, "E47.6.27", {"start": v(678.42, -209.94) * mm, "end": v(654.72, -250.99) * mm, "construction": true});
            skPoint(sketch, "E47.6.28", {"position": v(285.8, -363.63) * mm});
            skLineSegment(sketch, "E47.6.29", {"start": v(638.12, -231.43) * mm, "end": v(623.12, -257.41) * mm, "construction": true});
            skArc(sketch, "E47.6.30", {"start": v(318.05, -335.79) * mm, "mid": v(302.24, -350.08) * mm, "end": v(285.8, -363.63) * mm});
            skLineSegment(sketch, "E47.6.31", {"start": v(638.7, -368.75) * mm, "end": v(631.77, -364.75) * mm});
            skArc(sketch, "E47.6.32", {"start": v(312.48, -349.06) * mm, "mid": v(301.15, -358.89) * mm, "end": v(289.5, -368.35) * mm});
            skLineSegment(sketch, "E47.6.33", {"start": v(457.81, -65.7) * mm, "end": v(469.69, -67.4) * mm, "construction": true});
            skArc(sketch, "E47.6.34", {"start": v(469.69, -67.4) * mm, "mid": v(468.13, -77.47) * mm, "end": v(466.36, -87.5) * mm});
            skArc(sketch, "E47.6.35", {"start": v(463.75, -66.54) * mm, "mid": v(461.38, -81.36) * mm, "end": v(458.54, -96.09) * mm});
            skLineSegment(sketch, "E47.6.36", {"start": v(469.69, -67.4) * mm, "end": v(463.75, -66.54) * mm});
            skLineSegment(sketch, "E47.6.37", {"start": v(312.48, -349.06) * mm, "end": v(318.05, -355.28) * mm, "construction": true});
            skLineSegment(sketch, "E47.6.38", {"start": v(458.54, -96.09) * mm, "end": v(466.71, -97.8) * mm, "construction": true});
            skLineSegment(sketch, "E47.6.39", {"start": v(289.5, -368.35) * mm, "end": v(285.8, -363.63) * mm});
            skLineSegment(sketch, "E47.6.40", {"start": v(285.8, -363.63) * mm, "end": v(293.21, -373.07) * mm, "construction": true});
            skPoint(sketch, "E47.7.0", {"position": v(637.59, 232.89) * mm});
            skPoint(sketch, "E47.7.1", {"position": v(658.76, 251.92) * mm});
            skArc(sketch, "E47.7.2", {"start": v(726.3, 128.07) * mm, "mid": v(704.47, 184.56) * mm, "end": v(662.88, 228.58) * mm});
            skPoint(sketch, "E47.7.3", {"position": v(718.42, 126.68) * mm});
            skPoint(sketch, "E47.7.4", {"position": v(457.81, -65.69) * mm});
            skLineSegment(sketch, "E47.7.5", {"start": v(413.03, 221.14) * mm, "end": v(555.02, 146.35) * mm});
            skArc(sketch, "E47.7.6", {"start": v(413.03, 221.14) * mm, "mid": v(476.57, 213.1) * mm, "end": v(540.45, 217.86) * mm});
            skPoint(sketch, "E47.7.7", {"position": v(642.8, 203.34) * mm});
            skPoint(sketch, "E47.7.8", {"position": v(398.03, 247.12) * mm});
            skLineSegment(sketch, "E47.7.9", {"start": v(521.62, 215.1) * mm, "end": v(588.72, 179.77) * mm});
            skPoint(sketch, "E47.7.10", {"position": v(726.3, 128.07) * mm});
            skArc(sketch, "E47.7.11", {"start": v(665.14, 215.78) * mm, "mid": v(530.12, 99.1) * mm, "end": v(463.75, -66.54) * mm});
            skPoint(sketch, "E47.7.12", {"position": v(534.08, 254) * mm});
            skLineSegment(sketch, "E47.7.13", {"start": v(654.65, 275.26) * mm, "end": v(413.5, 232.74) * mm, "construction": true});
            skPoint(sketch, "E47.7.14", {"position": v(458.54, -96.08) * mm});
            skLineSegment(sketch, "E47.7.15", {"start": v(557.79, 149.42) * mm, "end": v(427.14, 218.22) * mm});
            skArc(sketch, "E47.7.16", {"start": v(640.2, 218.12) * mm, "mid": v(520.73, 102.08) * mm, "end": v(459.48, -52.8) * mm});
            skArc(sketch, "E47.7.17", {"start": v(662.88, 228.58) * mm, "mid": v(600.63, 235.6) * mm, "end": v(538.2, 230.66) * mm});
            skPoint(sketch, "E47.7.18", {"position": v(662.88, 228.58) * mm});
            skPoint(sketch, "E47.7.19", {"position": v(459.48, -52.8) * mm});
            skPoint(sketch, "E47.7.20", {"position": v(538.2, 230.66) * mm});
            skPoint(sketch, "E47.7.21", {"position": v(665.14, 215.78) * mm});
            skArc(sketch, "E47.7.22", {"start": v(640.2, 218.12) * mm, "mid": v(590.3, 222.28) * mm, "end": v(540.45, 217.86) * mm});
            skLineSegment(sketch, "E47.7.23", {"start": v(528.54, 215.99) * mm, "end": v(591.96, 182.59) * mm});
            skArc(sketch, "E47.7.24", {"start": v(413.5, 232.74) * mm, "mid": v(475.75, 225.72) * mm, "end": v(538.2, 230.66) * mm});
            skArc(sketch, "E47.7.25", {"start": v(718.42, 126.68) * mm, "mid": v(699.98, 176.14) * mm, "end": v(665.14, 215.78) * mm});
            skPoint(sketch, "E47.7.26", {"position": v(392.93, 243.95) * mm});
            skLineSegment(sketch, "E47.7.27", {"start": v(654.65, 275.26) * mm, "end": v(662.88, 228.58) * mm, "construction": true});
            skPoint(sketch, "E47.7.28", {"position": v(452.67, -94.85) * mm});
            skLineSegment(sketch, "E47.7.29", {"start": v(637.59, 232.89) * mm, "end": v(642.8, 203.34) * mm, "construction": true});
            skArc(sketch, "E47.7.30", {"start": v(459.48, -52.8) * mm, "mid": v(456.56, -73.9) * mm, "end": v(452.67, -94.85) * mm});
            skLineSegment(sketch, "E47.7.31", {"start": v(726.3, 128.07) * mm, "end": v(718.42, 126.68) * mm});
            skArc(sketch, "E47.7.32", {"start": v(463.75, -66.54) * mm, "mid": v(461.38, -81.35) * mm, "end": v(458.54, -96.08) * mm});
            skLineSegment(sketch, "E47.7.33", {"start": v(392.93, 243.95) * mm, "end": v(403.12, 250.28) * mm, "construction": true});
            skArc(sketch, "E47.7.34", {"start": v(403.12, 250.28) * mm, "mid": v(408.4, 241.56) * mm, "end": v(413.5, 232.74) * mm});
            skArc(sketch, "E47.7.35", {"start": v(398.03, 247.12) * mm, "mid": v(405.73, 234.25) * mm, "end": v(413.03, 221.14) * mm});
            skLineSegment(sketch, "E47.7.36", {"start": v(403.12, 250.28) * mm, "end": v(398.03, 247.12) * mm});
            skLineSegment(sketch, "E47.7.37", {"start": v(463.75, -66.54) * mm, "end": v(472.02, -67.72) * mm, "construction": true});
            skLineSegment(sketch, "E47.7.38", {"start": v(413.03, 221.14) * mm, "end": v(420.39, 225.08) * mm, "construction": true});
            skLineSegment(sketch, "E47.7.39", {"start": v(458.54, -96.08) * mm, "end": v(452.67, -94.85) * mm});
            skLineSegment(sketch, "E47.7.40", {"start": v(452.67, -94.85) * mm, "end": v(464.41, -97.31) * mm, "construction": true});
            skPoint(sketch, "E47.8.0", {"position": v(338.72, 588.24) * mm});
            skPoint(sketch, "E47.8.1", {"position": v(342.71, 616.42) * mm});
            skArc(sketch, "E47.8.2", {"start": v(474.06, 564.96) * mm, "mid": v(421.02, 594.2) * mm, "end": v(360.87, 601.2) * mm});
            skPoint(sketch, "E47.8.3", {"position": v(468.91, 558.83) * mm});
            skPoint(sketch, "E47.8.4", {"position": v(392.93, 243.96) * mm});
            skLineSegment(sketch, "E47.8.5", {"start": v(174.25, 434.89) * mm, "end": v(331.1, 468.87) * mm});
            skArc(sketch, "E47.8.6", {"start": v(174.25, 434.89) * mm, "mid": v(228.1, 469.57) * mm, "end": v(273.97, 514.28) * mm});
            skPoint(sketch, "E47.8.7", {"position": v(361.7, 568.95) * mm});
            skPoint(sketch, "E47.8.8", {"position": v(146.06, 445.15) * mm});
            skLineSegment(sketch, "E47.8.9", {"start": v(261.31, 500.07) * mm, "end": v(335.43, 516.13) * mm});
            skPoint(sketch, "E47.8.10", {"position": v(474.06, 564.96) * mm});
            skArc(sketch, "E47.8.11", {"start": v(370.82, 592.84) * mm, "mid": v(342.39, 416.67) * mm, "end": v(398.02, 247.12) * mm});
            skPoint(sketch, "E47.8.12", {"position": v(245.86, 537.87) * mm});
            skLineSegment(sketch, "E47.8.13", {"start": v(324.56, 631.66) * mm, "end": v(167.16, 444.08) * mm, "construction": true});
            skPoint(sketch, "E47.8.14", {"position": v(413.02, 221.14) * mm});
            skLineSegment(sketch, "E47.8.15", {"start": v(331.25, 473) * mm, "end": v(186.94, 441.73) * mm});
            skArc(sketch, "E47.8.16", {"start": v(350.21, 578.6) * mm, "mid": v(333.29, 412.91) * mm, "end": v(385.91, 254.9) * mm});
            skArc(sketch, "E47.8.17", {"start": v(360.87, 601.2) * mm, "mid": v(308.67, 566.56) * mm, "end": v(264.01, 522.64) * mm});
            skPoint(sketch, "E47.8.18", {"position": v(360.87, 601.2) * mm});
            skPoint(sketch, "E47.8.19", {"position": v(385.91, 254.9) * mm});
            skPoint(sketch, "E47.8.20", {"position": v(264.01, 522.64) * mm});
            skPoint(sketch, "E47.8.21", {"position": v(370.82, 592.84) * mm});
            skArc(sketch, "E47.8.22", {"start": v(350.21, 578.6) * mm, "mid": v(309.32, 549.72) * mm, "end": v(273.97, 514.28) * mm});
            skLineSegment(sketch, "E47.8.23", {"start": v(266.05, 505.2) * mm, "end": v(336.1, 520.37) * mm});
            skArc(sketch, "E47.8.24", {"start": v(167.16, 444.08) * mm, "mid": v(219.35, 478.71) * mm, "end": v(264.01, 522.64) * mm});
            skArc(sketch, "E47.8.25", {"start": v(468.91, 558.83) * mm, "mid": v(423, 584.87) * mm, "end": v(370.82, 592.84) * mm});
            skPoint(sketch, "E47.8.26", {"position": v(144.2, 439.45) * mm});
            skLineSegment(sketch, "E47.8.27", {"start": v(324.56, 631.66) * mm, "end": v(360.87, 601.2) * mm, "construction": true});
            skPoint(sketch, "E47.8.28", {"position": v(407.73, 218.31) * mm});
            skLineSegment(sketch, "E47.8.29", {"start": v(338.72, 588.24) * mm, "end": v(361.7, 568.95) * mm, "construction": true});
            skArc(sketch, "E47.8.30", {"start": v(385.91, 254.9) * mm, "mid": v(397.25, 236.86) * mm, "end": v(407.73, 218.31) * mm});
            skLineSegment(sketch, "E47.8.31", {"start": v(474.06, 564.96) * mm, "end": v(468.91, 558.83) * mm});
            skArc(sketch, "E47.8.32", {"start": v(398.02, 247.12) * mm, "mid": v(405.73, 234.25) * mm, "end": v(413.02, 221.14) * mm});
            skLineSegment(sketch, "E47.8.33", {"start": v(144.2, 439.45) * mm, "end": v(147.93, 450.85) * mm, "construction": true});
            skArc(sketch, "E47.8.34", {"start": v(147.93, 450.85) * mm, "mid": v(157.58, 447.57) * mm, "end": v(167.16, 444.08) * mm});
            skArc(sketch, "E47.8.35", {"start": v(146.06, 445.15) * mm, "mid": v(160.24, 440.24) * mm, "end": v(174.25, 434.89) * mm});
            skLineSegment(sketch, "E47.8.36", {"start": v(147.93, 450.85) * mm, "end": v(146.06, 445.15) * mm});
            skLineSegment(sketch, "E47.8.37", {"start": v(398.02, 247.12) * mm, "end": v(405.12, 251.53) * mm, "construction": true});
            skLineSegment(sketch, "E47.8.38", {"start": v(174.25, 434.89) * mm, "end": v(177.36, 442.64) * mm, "construction": true});
            skLineSegment(sketch, "E47.8.39", {"start": v(413.02, 221.14) * mm, "end": v(407.73, 218.31) * mm});
            skLineSegment(sketch, "E47.8.40", {"start": v(407.73, 218.31) * mm, "end": v(418.31, 223.97) * mm, "construction": true});
            skSolve(sketch);
        }
        {
            var Q0;
            {var subQ15=sQuery(id+"F0.wireOp",EDGE,"E10");Q0=makeQuery(id+"F0.imprint","IMPRINT",FACE,{"disambiguationData":[TD([[makeQuery(id+"F0.imprint","IMPRINT",EDGE,{"derivedFrom":subQ15}),1.0]])]});}
            var Q1;
            {var subQ0=sQuery(id+"F0.wireOp",EDGE,"E45");Q1=makeQuery(id+"F0.imprint","IMPRINT",FACE,{"disambiguationData":[TD([[makeQuery(id+"F0.imprint","IMPRINT",EDGE,{"derivedFrom":subQ0}),1.0]])]});}
            var Q2;
            Q2=makeQuery(id+"F0.imprint","IMPRINT",FACE,{"disambiguationData":[TD([[makeQuery(id+"F0.imprint","IMPRINT",EDGE,{"derivedFrom":sQuery(id+"F0.wireOp",EDGE,"E47.8.2")}),1.0]])]});
            var Q3;
            {var subQ0=sQuery(id+"F0.wireOp",EDGE,"E47.8.9");Q3=makeQuery(id+"F0.imprint","IMPRINT",FACE,{"disambiguationData":[TD([[makeQuery(id+"F0.imprint","IMPRINT",EDGE,{"derivedFrom":subQ0}),1.0]])]});}
            var Q4;
            {var subQ0=sQuery(id+"F0.wireOp",EDGE,"E47.8.5");Q4=makeQuery(id+"F0.imprint","IMPRINT",FACE,{"disambiguationData":[TD([[makeQuery(id+"F0.imprint","IMPRINT",EDGE,{"derivedFrom":subQ0}),1.0]])]});}
            var Q5;
            Q5=makeQuery(id+"F0.imprint","IMPRINT",FACE,{"disambiguationData":[TD([[makeQuery(id+"F0.imprint","IMPRINT",EDGE,{"derivedFrom":sQuery(id+"F0.wireOp",EDGE,"E47.7.2")}),1.0]])]});
            var Q6;
            {var subQ0=sQuery(id+"F0.wireOp",EDGE,"E47.7.9");Q6=makeQuery(id+"F0.imprint","IMPRINT",FACE,{"disambiguationData":[TD([[makeQuery(id+"F0.imprint","IMPRINT",EDGE,{"derivedFrom":subQ0}),1.0]])]});}
            var Q7;
            {var subQ0=sQuery(id+"F0.wireOp",EDGE,"E47.7.5");Q7=makeQuery(id+"F0.imprint","IMPRINT",FACE,{"disambiguationData":[TD([[makeQuery(id+"F0.imprint","IMPRINT",EDGE,{"derivedFrom":subQ0}),1.0]])]});}
            var Q8;
            Q8=makeQuery(id+"F0.imprint","IMPRINT",FACE,{"disambiguationData":[TD([[makeQuery(id+"F0.imprint","IMPRINT",EDGE,{"derivedFrom":sQuery(id+"F0.wireOp",EDGE,"E47.6.2")}),1.0]])]});
            var Q9;
            {var subQ0=sQuery(id+"F0.wireOp",EDGE,"E47.6.5");Q9=makeQuery(id+"F0.imprint","IMPRINT",FACE,{"disambiguationData":[TD([[makeQuery(id+"F0.imprint","IMPRINT",EDGE,{"derivedFrom":subQ0}),1.0]])]});}
            var Q10;
            {var subQ0=sQuery(id+"F0.wireOp",EDGE,"E47.6.9");Q10=makeQuery(id+"F0.imprint","IMPRINT",FACE,{"disambiguationData":[TD([[makeQuery(id+"F0.imprint","IMPRINT",EDGE,{"derivedFrom":subQ0}),1.0]])]});}
            var Q11;
            Q11=makeQuery(id+"F0.imprint","IMPRINT",FACE,{"disambiguationData":[TD([[makeQuery(id+"F0.imprint","IMPRINT",EDGE,{"derivedFrom":sQuery(id+"F0.wireOp",EDGE,"E47.5.2")}),1.0]])]});
            var Q12;
            {var subQ0=sQuery(id+"F0.wireOp",EDGE,"E47.5.9");Q12=makeQuery(id+"F0.imprint","IMPRINT",FACE,{"disambiguationData":[TD([[makeQuery(id+"F0.imprint","IMPRINT",EDGE,{"derivedFrom":subQ0}),1.0]])]});}
            var Q13;
            {var subQ0=sQuery(id+"F0.wireOp",EDGE,"E47.5.5");Q13=makeQuery(id+"F0.imprint","IMPRINT",FACE,{"disambiguationData":[TD([[makeQuery(id+"F0.imprint","IMPRINT",EDGE,{"derivedFrom":subQ0}),1.0]])]});}
            var Q14;
            Q14=makeQuery(id+"F0.imprint","IMPRINT",FACE,{"disambiguationData":[TD([[makeQuery(id+"F0.imprint","IMPRINT",EDGE,{"derivedFrom":sQuery(id+"F0.wireOp",EDGE,"E47.4.2")}),1.0]])]});
            var Q15;
            {var subQ0=sQuery(id+"F0.wireOp",EDGE,"E47.4.9");Q15=makeQuery(id+"F0.imprint","IMPRINT",FACE,{"disambiguationData":[TD([[makeQuery(id+"F0.imprint","IMPRINT",EDGE,{"derivedFrom":subQ0}),1.0]])]});}
            var Q16;
            {var subQ0=sQuery(id+"F0.wireOp",EDGE,"E47.4.5");Q16=makeQuery(id+"F0.imprint","IMPRINT",FACE,{"disambiguationData":[TD([[makeQuery(id+"F0.imprint","IMPRINT",EDGE,{"derivedFrom":subQ0}),1.0]])]});}
            var Q17;
            Q17=makeQuery(id+"F0.imprint","IMPRINT",FACE,{"disambiguationData":[TD([[makeQuery(id+"F0.imprint","IMPRINT",EDGE,{"derivedFrom":sQuery(id+"F0.wireOp",EDGE,"E47.3.2")}),1.0]])]});
            var Q18;
            {var subQ0=sQuery(id+"F0.wireOp",EDGE,"E47.3.9");Q18=makeQuery(id+"F0.imprint","IMPRINT",FACE,{"disambiguationData":[TD([[makeQuery(id+"F0.imprint","IMPRINT",EDGE,{"derivedFrom":subQ0}),1.0]])]});}
            var Q19;
            {var subQ0=sQuery(id+"F0.wireOp",EDGE,"E47.3.5");Q19=makeQuery(id+"F0.imprint","IMPRINT",FACE,{"disambiguationData":[TD([[makeQuery(id+"F0.imprint","IMPRINT",EDGE,{"derivedFrom":subQ0}),1.0]])]});}
            var Q20;
            Q20=makeQuery(id+"F0.imprint","IMPRINT",FACE,{"disambiguationData":[TD([[makeQuery(id+"F0.imprint","IMPRINT",EDGE,{"derivedFrom":sQuery(id+"F0.wireOp",EDGE,"E47.2.2")}),1.0]])]});
            var Q21;
            {var subQ0=sQuery(id+"F0.wireOp",EDGE,"E47.2.9");Q21=makeQuery(id+"F0.imprint","IMPRINT",FACE,{"disambiguationData":[TD([[makeQuery(id+"F0.imprint","IMPRINT",EDGE,{"derivedFrom":subQ0}),1.0]])]});}
            var Q22;
            {var subQ0=sQuery(id+"F0.wireOp",EDGE,"E47.2.5");Q22=makeQuery(id+"F0.imprint","IMPRINT",FACE,{"disambiguationData":[TD([[makeQuery(id+"F0.imprint","IMPRINT",EDGE,{"derivedFrom":subQ0}),1.0]])]});}
            var Q23;
            Q23=makeQuery(id+"F0.imprint","IMPRINT",FACE,{"disambiguationData":[TD([[makeQuery(id+"F0.imprint","IMPRINT",EDGE,{"derivedFrom":sQuery(id+"F0.wireOp",EDGE,"E47.1.2")}),1.0]])]});
            var Q24;
            {var subQ0=sQuery(id+"F0.wireOp",EDGE,"E47.1.5");Q24=makeQuery(id+"F0.imprint","IMPRINT",FACE,{"disambiguationData":[TD([[makeQuery(id+"F0.imprint","IMPRINT",EDGE,{"derivedFrom":subQ0}),1.0]])]});}
            var Q25;
            {var subQ0=sQuery(id+"F0.wireOp",EDGE,"E47.1.9");Q25=makeQuery(id+"F0.imprint","IMPRINT",FACE,{"disambiguationData":[TD([[makeQuery(id+"F0.imprint","IMPRINT",EDGE,{"derivedFrom":subQ0}),1.0]])]});}
            var Q26;
            {var subQ0=sQuery(id+"F0.wireOp",EDGE,"E43");Q26=makeQuery(id+"F0.imprint","IMPRINT",FACE,{"disambiguationData":[TD([[makeQuery(id+"F0.imprint","IMPRINT",EDGE,{"derivedFrom":subQ0}),1.0]])]});}
            extrude(context, id + "F1", {"entities" : qUnion([Q0, Q1, Q2, Q3, Q4, Q5, Q6, Q7, Q8, Q9, Q10, Q11, Q12, Q13, Q14, Q15, Q16, Q17, Q18, Q19, Q20, Q21, Q22, Q23, Q24, Q25, Q26]), "depth" : 4840 * mm});
        }
    });
